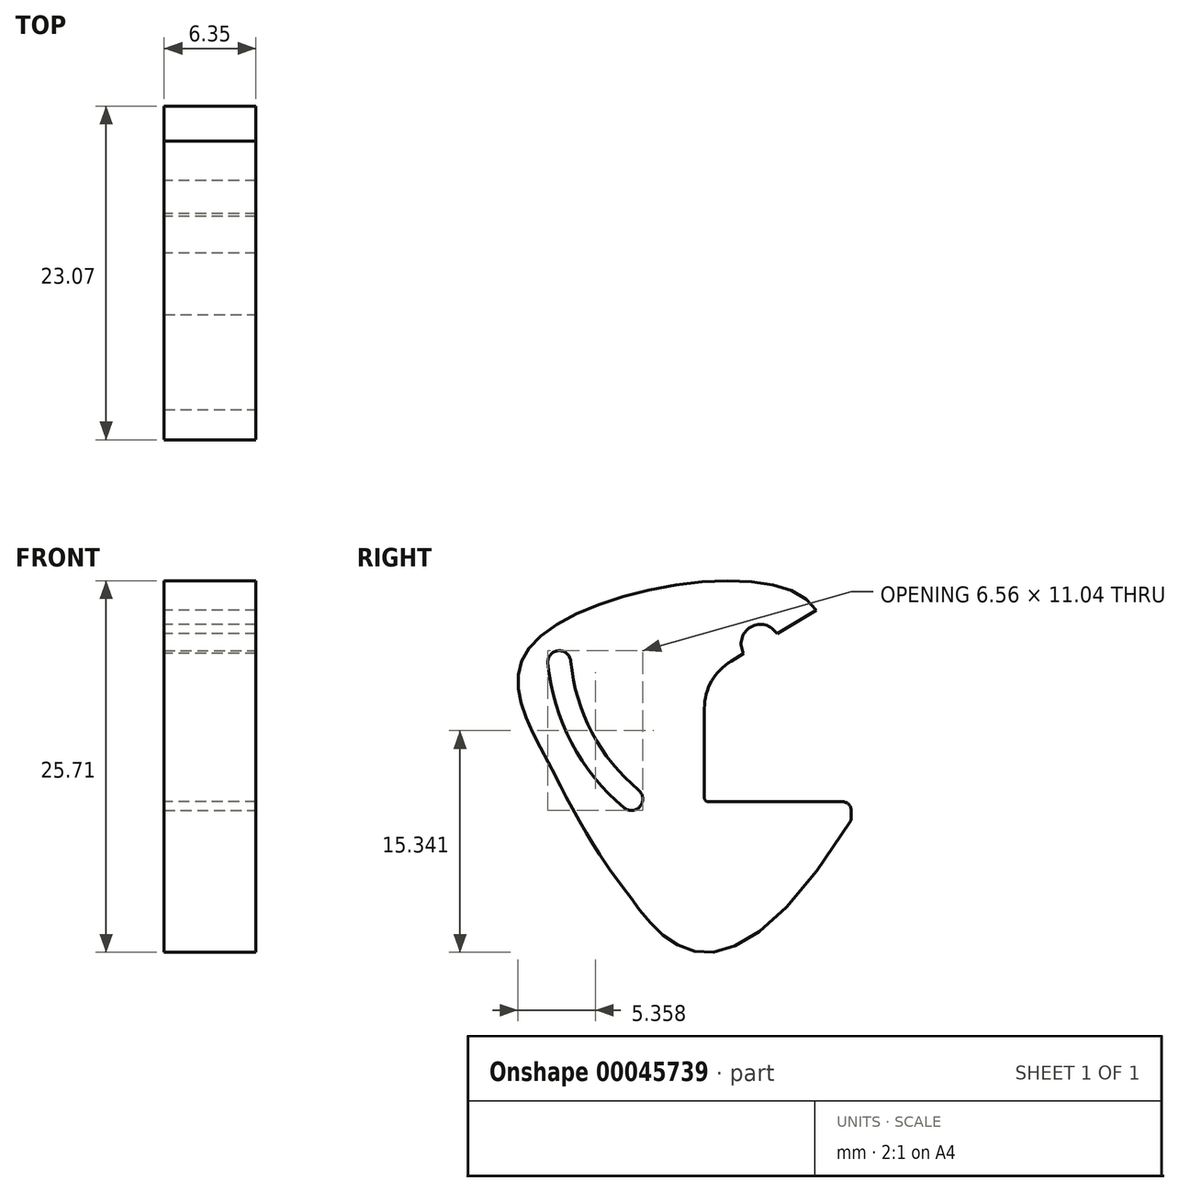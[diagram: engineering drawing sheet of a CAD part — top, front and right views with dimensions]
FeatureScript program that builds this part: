
annotation { "Feature Type Name" : "Feature", "Feature Type Description" : "" }
export const myFeature = defineFeature(function(context is Context, id is Id, definition is map)
    precondition{}
    {
        {
            var Q0;
            Q0=qCreatedBy(makeId("Right.planeOp"),FACE);
            var sketch = newSketch(context, id + "F0", { "sketchPlane" : qUnion([Q0])});
            skLineSegment(sketch, "E0", {"start": v(-3.87, -10.92) * mm, "end": v(6.29, -10.92) * mm});
            skLineSegment(sketch, "E1", {"start": v(6.29, -10.92) * mm, "end": v(6.29, -10.92) * mm});
            skLineSegment(sketch, "E2", {"start": v(6.29, -10.92) * mm, "end": v(-3.87, -10.92) * mm, "construction": true});
            skPoint(sketch, "E3", {"position": v(2.8, -10.92) * mm});
            skLineSegment(sketch, "E4", {"start": v(2.8, -10.92) * mm, "end": v(2.8, 1.49) * mm, "construction": true});
            skLineSegment(sketch, "E5", {"start": v(0, 0) * mm, "end": v(2.8, 0) * mm, "construction": true});
            skCircle(sketch, "E6", {"center": v(0, 0) * mm, "radius": 1.33 * mm});
            skLineSegment(sketch, "E7", {"start": v(-3.87, -2.3) * mm, "end": v(-3.87, -2.3) * mm});
            skLineSegment(sketch, "E8", {"start": v(3.87, 2.3) * mm, "end": v(-3.87, -2.3) * mm});
            skArc(sketch, "E9", {"start": v(3.87, 2.3) * mm, "mid": v(2.3, -3.87) * mm, "end": v(-3.87, -2.3) * mm});
            skLineSegment(sketch, "E10", {"start": v(-3.87, -2.3) * mm, "end": v(-3.87, -10.92) * mm});
            skFitSpline(sketch, "E11", {"points": [v(6.51, -11.83) * mm, v(-8.94, -17.62) * mm, v(-11.33, -14.26) * mm, v(-14.14, -9.22) * mm], "startDerivative": vector(-56.6, -92.74) * mm, "endDerivative": vector(-6.01, 12.63) * mm});
            skPoint(sketch, "E12", {"position": v(6.29, -10.92) * mm});
            skLineSegment(sketch, "E13", {"start": v(6.29, -10.92) * mm, "end": v(-0.7, -10.92) * mm, "construction": true});
            skLineSegment(sketch, "E14", {"start": v(-0.7, 80.5) * mm, "end": v(6.29, 80.5) * mm, "construction": true});
            skPoint(sketch, "E15", {"position": v(2.8, 80.5) * mm});
            skFitSpline(sketch, "E16", {"points": [v(3.87, 2.3) * mm, v(-15.76, 0) * mm, v(-14.14, -9.22) * mm], "startDerivative": vector(-12.06, 20.24) * mm, "endDerivative": vector(11.9, -23.33) * mm});
            skLineSegment(sketch, "E17", {"start": v(-3.87, -10.92) * mm, "end": v(-3.87, -15.9) * mm, "construction": true});
            skLineSegment(sketch, "E18", {"start": v(6.29, -10.92) * mm, "end": v(6.29, -12.2) * mm});
            skSolve(sketch);
        }
        {
            var Q0;
            {var subQ0=sQuery(id+"F0.wireOp",EDGE,"E9");Q0=makeQuery(id+"F0.imprint","IMPRINT",FACE,{"disambiguationData":[TD([[makeQuery(id+"F0.imprint","IMPRINT",EDGE,{"derivedFrom":subQ0}),-1.0]])]});}
            var Q1;
            {var subQ3=sQuery(id+"F0.wireOp",EDGE,"E10");Q1=makeQuery(id+"F0.imprint","IMPRINT",FACE,{"disambiguationData":[TD([[makeQuery(id+"F0.imprint","IMPRINT",EDGE,{"derivedFrom":subQ3}),-1.0]])]});}
            extrude(context, id + "F1", {"entities" : qUnion([Q0, Q1]), "depth" : 6.35 * mm});
        }
        {
            var Q0;
            Q0=makeQuery(id+"F1.opExtrude","SWEPT_EDGE",EDGE,{"disambiguationData":[OSD([sQuery(id+"F0.wireOp",EDGE,"E7"),sQuery(id+"F0.wireOp",EDGE,"E10")])]});
            var Q1;
            Q1=makeQuery(id+"F1.opExtrude","SWEPT_EDGE",EDGE,{"disambiguationData":[OSD([sQuery(id+"F0.wireOp",EDGE,"E0"),sQuery(id+"F0.wireOp",EDGE,"E10")])]});
            fillet(context, id + "F2", {"entities" : qUnion([Q0, Q1]), "radius" : 0.25 * mm, "tangentPropagation" : true, "allowEdgeOverflow" : false});
        }
        {
            var Q0;
            Q0=makeQuery(id+"F1.opExtrude","CAP_FACE",FACE,{"disambiguationData":[OSD([sQuery(id+"F0.wireOp",EDGE,"E0"),sQuery(id+"F0.wireOp",EDGE,"E6"),sQuery(id+"F0.wireOp",EDGE,"567ba700-bead-46c1-8d2c-5112f4104d21"),sQuery(id+"F0.wireOp",EDGE,"E7"),sQuery(id+"F0.wireOp",EDGE,"E9"),sQuery(id+"F0.wireOp",EDGE,"E10"),sQuery(id+"F0.wireOp",EDGE,"9bc204e8-18d8-4747-ae06-27320a8a0a8e"),sQuery(id+"F0.wireOp",EDGE,"E11")])],"isStart":false});
            var sketch = newSketch(context, id + "F3", { "sketchPlane" : qUnion([Q0])});
            skArc(sketch, "E19", {"start": v(-13.12, -1.2) * mm, "mid": v(-11.66, -6.13) * mm, "end": v(-8.43, -10.13) * mm});
            skArc(sketch, "E20", {"start": v(-14.7, -1.35) * mm, "mid": v(-13.07, -6.87) * mm, "end": v(-9.44, -11.35) * mm});
            skLineSegment(sketch, "E21", {"start": v(0, 0) * mm, "end": v(-9.44, -11.35) * mm, "construction": true});
            skLineSegment(sketch, "E22", {"start": v(0, 0) * mm, "end": v(-14.7, -1.35) * mm, "construction": true});
            skArc(sketch, "E23", {"start": v(-13.12, -1.2) * mm, "mid": v(-13.98, -0.49) * mm, "end": v(-14.7, -1.35) * mm});
            skArc(sketch, "E24", {"start": v(-8.43, -10.13) * mm, "mid": v(-8.32, -11.25) * mm, "end": v(-9.44, -11.35) * mm});
            skSolve(sketch);
        }
        {
            var Q0;
            Q0=makeQuery(id+"F3.imprint","IMPRINT",FACE,{"disambiguationData":[TD([[makeQuery(id+"F3.imprint","IMPRINT",EDGE,{"derivedFrom":sQuery(id+"F3.wireOp",EDGE,"E19")}),-1.0]])]});
            extrude(context, id + "F4", {"entities" : qUnion([Q0]), "operationType" : NewBodyOperationType.REMOVE, "endBound" : BoundingType.UP_TO_NEXT, "oppositeDirection" : true, "depth" : 25.4 * mm});
        }
        {
            var Q0;
            Q0=makeQuery(id+"F1.opExtrude","SWEPT_EDGE",EDGE,{"disambiguationData":[OSD([sQuery(id+"F0.wireOp",EDGE,"E8"),sQuery(id+"F0.wireOp",EDGE,"E9"),sQuery(id+"F0.wireOp",EDGE,"E10")])]});
            fillet(context, id + "F5", {"entities" : qUnion([Q0]), "radius" : 3.8 * mm, "tangentPropagation" : true, "allowEdgeOverflow" : false});
        }
        {
            var Q0;
            Q0=makeQuery(id+"F1.opExtrude","SWEPT_EDGE",EDGE,{"disambiguationData":[OSD([sQuery(id+"F0.wireOp",EDGE,"E11"),sQuery(id+"F0.wireOp",EDGE,"91036f97-88cd-4fb1-9d25-dfc3fbba5263")])]});
            fillet(context, id + "F6", {"entities" : qUnion([Q0]), "radius" : 0.64 * mm, "tangentPropagation" : true, "allowEdgeOverflow" : false});
        }
        {
            var Q0;
            Q0=makeQuery(id+"F1.opExtrude","SWEPT_EDGE",EDGE,{"disambiguationData":[OSD([sQuery(id+"F0.wireOp",EDGE,"E0"),sQuery(id+"F0.wireOp",EDGE,"E18")])]});
            fillet(context, id + "F7", {"entities" : qUnion([Q0]), "radius" : 0.64 * mm, "tangentPropagation" : true, "allowEdgeOverflow" : false});
        }
    });
